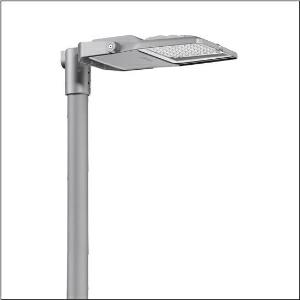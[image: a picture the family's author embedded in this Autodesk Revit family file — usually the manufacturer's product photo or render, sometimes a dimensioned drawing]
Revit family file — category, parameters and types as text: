
# Revit family: floodlight_fl_21_iq_mini___pl61_5xa7771d2c3a_41a8
name_source: partatom
category: Lighting Fixtures
units: mm (PartAtom-declared; Revit-internal decimal feet)

## family parameters
Cut with Voids When Loaded = No
Host = Face
Light Source = No
Part Type = Normal
Room Calculation Point = No
Round Connector Dimension = Use Diameter
Shared = No

## types (1)
- --- (1 x LED, 17500 lm, 143 W, 3000K)
    Apparent Load = 143 VA
    CIE Flux Codes = 33 65 98 100 100
    Color Rendering = 70
    Color Temperature = 3000K
    Default Elevation = 1800 mm
    Description = Floodlight FL 21 iQ mini, floodlight, primary light control with lens, of PMMA, primary optical cover: protective disc, of toughened safety glass, transparent, light distribution: PL61, light emission: direct distribution, installation type: surface-mounted, LED, High Power LED, rated luminous flux: 17.500lm, luminous efficacy: 122lm/W, light colour: 730, colour temperature: 3000K, control: Auto-Match, Temp-Guard, Lumen-Switch, Night-Set, Smart-Wire, Light-Fading, Desk-Remote (wireless, voltage-free reading and setting of iQ features in the workshop via application-optimized NFC function/RFID function), optimised constant luminous flux control (CLO 2.0), with terminal, 6-pole, mains connection: 220..240V, AC, 50/60Hz, start of lifetime: 143W, end of service life: 152W, reduction: 61W, luminaire housing, of diecast aluminium, powder-coated, Siteco® metallic grey (DB 702S), corrosivity category C5 mid according to DIN EN ISO 12944, sealing non-destructively replaceable, please order mast flange separately, mast bracket, of steel, galvanised, powder-coated, Siteco® metallic grey (DB 702S), protection rating (complete): IP66, insulation class (complete): insulation class II (safety insulation), certification: CE, ENEC, VDE, protection symbol: D, impact resistance: IK08, permissible operating ambient temperature: -40..+40°C, permissible operating ambient temperature for outdoor applications: -40..+50°C, standard: DIN EN 12944, LABS conformity tested according to VDMA 24364:2018-05, packaging unit: 1 piece

Light Distribution: PL61
    Height = 70 mm
    Lamp = 1 x LED
    Lamp Light Flux = 17500 lm
    Lamp Power = 143 W
    Lamp count = 1
    Length = 485 mm
    Luminous efficacy = 122 lm/W
    Manufacturer = Siteco
    ModVariant = No
    Model = 5XA7771D2C3A
    Number of Poles = 1
    OnlyDefault = Yes
    Power Factor = 1
    Product Name = Floodlight FL 21 iQ mini | PL61
    Product group = floodlight | pylon annexe
    ProductGroupID = 6200
    Protection Class = Protection class II
    Protection Degree = IP 66
    RLX_Detail_Level = 1
    RLX_Emergency_Light_Flux = 0 lm
    RLX_Emergency_Type = 0
    RLX_Emergency_Type_DB = No
    RlxData = <blob elided: 101633 chars, md5=ae5f9fa4>
    Socket = socket
    Standby Power = 0 W
    System Light Flux = 17500 lm
    System Power = 143 W
    Type Comments = factory setting: luminous flux: 100 % | dim-lin: 254 | 730 mA
    Type Image = l_1007125.jpg
    URL = http://relux.com
    VarID = @adj_123645
    Voltage = 0 V
    Weight = 0.00 kg
    Width = 337 mm

## geometry (parser evidence)
native form markers: Blend x4, Sweep x12
no freeform markers — native parametric forms only
